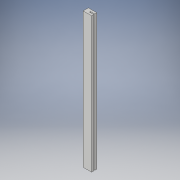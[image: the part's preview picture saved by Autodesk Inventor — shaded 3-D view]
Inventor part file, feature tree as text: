
AUTODESK INVENTOR PART (.ipt)
format: ipt  version: 2017 (Build 210142000, 142)  size: 102,400 bytes
history: native  units: in
note: dims shown in document units (in); Inventor stores cm internally (conversion verified against a paired STEP export)
features: extrude x1, sketch x1
ambient origin geometry x8: Origin, YZ Plane, XZ Plane, XY Plane, X Axis, Y Axis, Z Axis, Center Point
bodies: Solid1 (feature_tree)
feature tree (2):
  extrude  "Extrusion1"  Depth=0.25in
  sketch  "Sketch1"  dims[d0=1.0in d1=0.25in d2=0.5in d3=0.125in d4=1.0in d5=0.25in d6=16.0in d7=0.0in]
